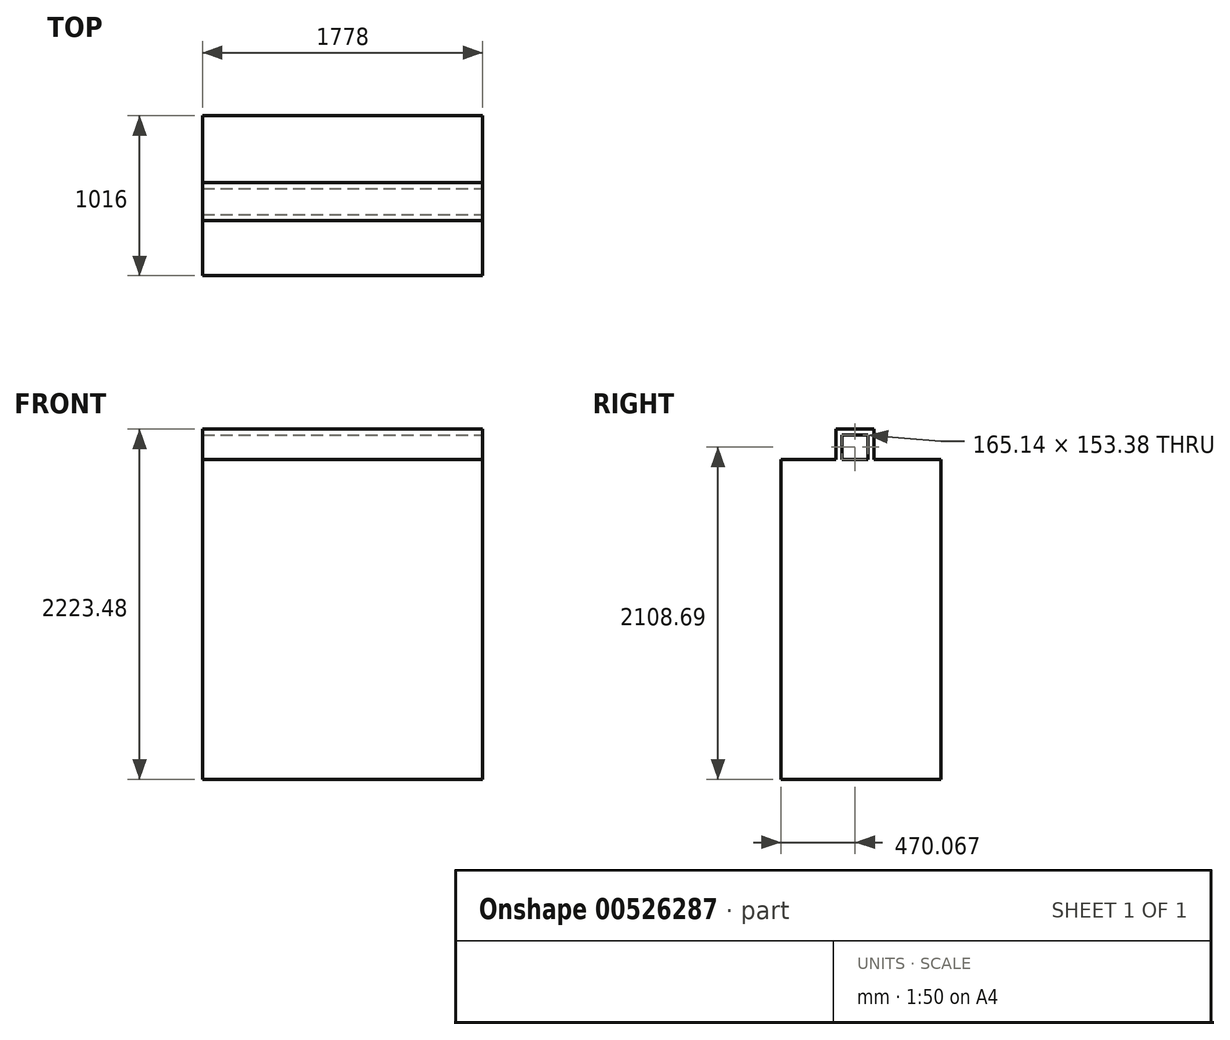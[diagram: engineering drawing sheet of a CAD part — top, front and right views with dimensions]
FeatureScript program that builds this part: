
annotation { "Feature Type Name" : "Feature", "Feature Type Description" : "" }
export const myFeature = defineFeature(function(context is Context, id is Id, definition is map)
    precondition{}
    {
        {
            var Q0;
            Q0=qCreatedBy(makeId("Right.planeOp"),FACE);
            var sketch = newSketch(context, id + "F0", { "sketchPlane" : qUnion([Q0])});
            skLineSegment(sketch, "E0.bottom", {"start": v(-501.1, 1086.4) * mm, "end": v(514.9, 1086.4) * mm});
            skLineSegment(sketch, "E0.top", {"start": v(-501.1, -945.6) * mm, "end": v(514.9, -945.6) * mm});
            skLineSegment(sketch, "E0.left", {"start": v(-501.1, 1086.4) * mm, "end": v(-501.1, -945.6) * mm});
            skLineSegment(sketch, "E0.right", {"start": v(514.9, 1086.4) * mm, "end": v(514.9, -945.6) * mm});
            skSolve(sketch);
        }
        {
            var Q0;
            Q0 = qSketchRegion(id + "F0", true);
            extrude(context, id + "F1", {"entities" : qUnion([Q0]), "depth" : 1778 * mm, "offsetDistance" : 25.4 * mm});
        }
        {
            var Q0;
            Q0=makeQuery(id+"F1.opExtrude","CAP_FACE",FACE,{"disambiguationData":[OSD([sQuery(id+"F0.wireOp",EDGE,"E0.bottom"),sQuery(id+"F0.wireOp",EDGE,"E0.top"),sQuery(id+"F0.wireOp",EDGE,"E0.left"),sQuery(id+"F0.wireOp",EDGE,"E0.right")])],"isStart":false});
            var sketch = newSketch(context, id + "F2", { "sketchPlane" : qUnion([Q0])});
            skLineSegment(sketch, "E1", {"start": v(-113.6, 1021.07) * mm, "end": v(-113.6, 1239.77) * mm});
            skLineSegment(sketch, "E2", {"start": v(-113.6, 1239.77) * mm, "end": v(51.54, 1239.77) * mm});
            skLineSegment(sketch, "E3", {"start": v(51.54, 1239.77) * mm, "end": v(51.54, 1034.46) * mm});
            skLineSegment(sketch, "E4.0", {"start": v(89.64, 1277.87) * mm, "end": v(89.64, 1034.46) * mm});
            skLineSegment(sketch, "E4.1", {"start": v(-151.7, 1277.87) * mm, "end": v(89.64, 1277.87) * mm});
            skLineSegment(sketch, "E4.2", {"start": v(-151.7, 1021.07) * mm, "end": v(-151.7, 1277.87) * mm});
            skSolve(sketch);
        }
        {
            var Q0;
            {var subQ5=sQuery(id+"F2.wireOp",EDGE,"E2");Q0=makeQuery(id+"F2.imprint","IMPRINT",FACE,{"disambiguationData":[TD([[makeQuery(id+"F2.imprint","IMPRINT",EDGE,{"derivedFrom":subQ5}),1.0]])]});}
            extrude(context, id + "F3", {"entities" : qUnion([Q0]), "operationType" : NewBodyOperationType.ADD, "oppositeDirection" : true, "depth" : 1778 * mm, "offsetDistance" : 25.4 * mm});
        }
    });
